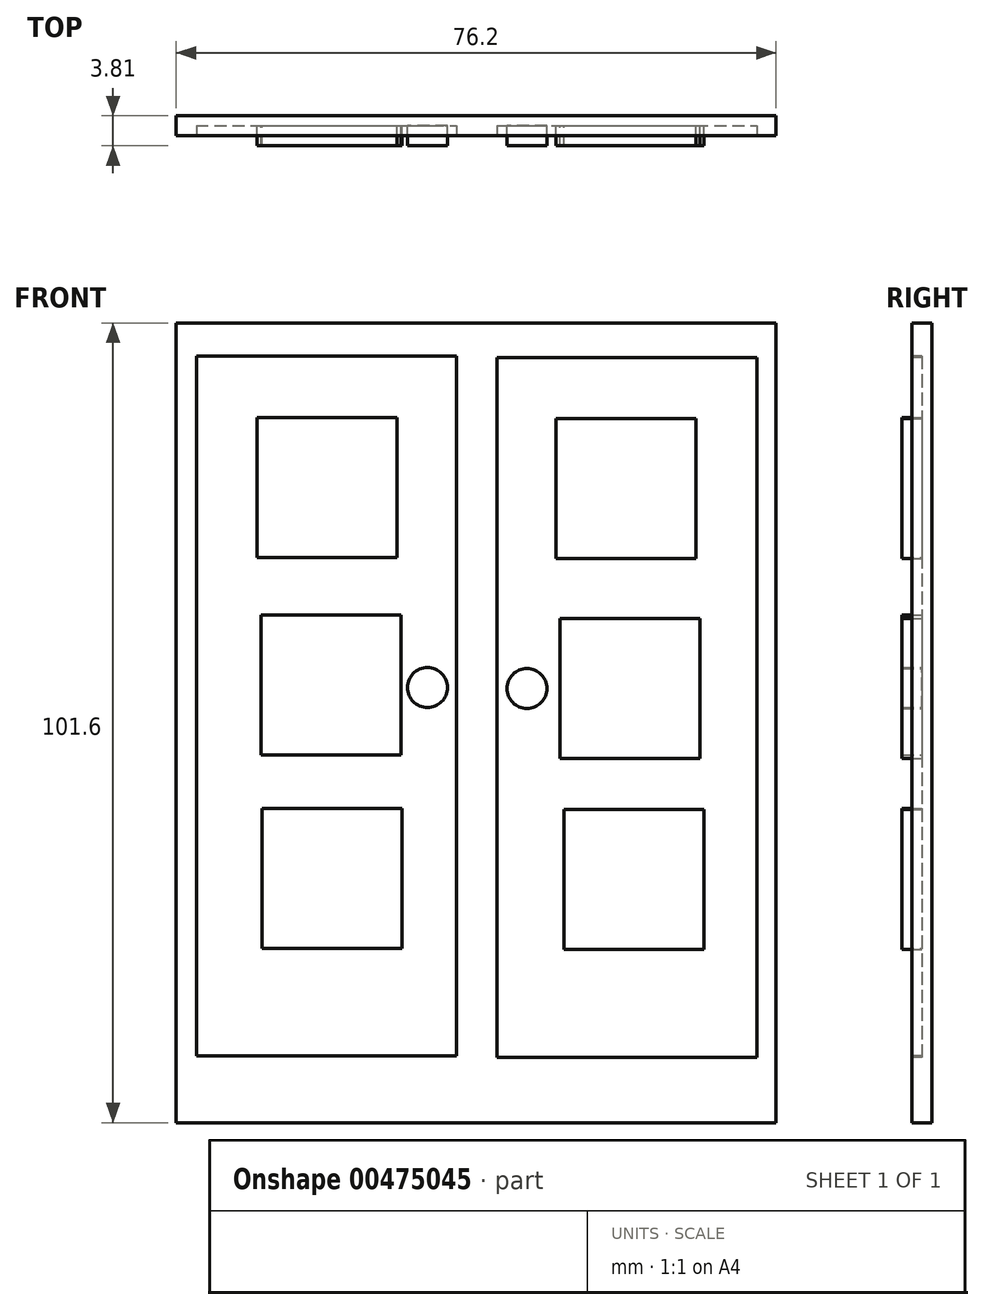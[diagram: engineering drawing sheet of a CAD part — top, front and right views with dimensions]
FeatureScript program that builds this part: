
annotation { "Feature Type Name" : "Feature", "Feature Type Description" : "" }
export const myFeature = defineFeature(function(context is Context, id is Id, definition is map)
    precondition{}
    {
        {
            var Q0;
            Q0=qCreatedBy(makeId("Front.planeOp"),FACE);
            var sketch = newSketch(context, id + "F0", { "sketchPlane" : qUnion([Q0])});
            skLineSegment(sketch, "E0.bottom", {"start": v(-36.76, -60.42) * mm, "end": v(39.44, -60.42) * mm});
            skLineSegment(sketch, "E0.top", {"start": v(-36.76, 41.18) * mm, "end": v(39.44, 41.18) * mm});
            skLineSegment(sketch, "E0.left", {"start": v(-36.76, -60.42) * mm, "end": v(-36.76, 41.18) * mm});
            skLineSegment(sketch, "E0.right", {"start": v(39.44, -60.42) * mm, "end": v(39.44, 41.18) * mm});
            skSolve(sketch);
        }
        {
            var Q0;
            Q0=qSketchRegion(id+"F0",true);
            extrude(context, id + "F1", {"entities" : qUnion([Q0]), "depth" : 2.54 * mm});
        }
        {
            var Q0;
            Q0=makeQuery(id+"F1.opExtrude","CAP_FACE",FACE,{"disambiguationData":[OSD([sQuery(id+"F0.wireOp",EDGE,"E0.bottom"),sQuery(id+"F0.wireOp",EDGE,"E0.top"),sQuery(id+"F0.wireOp",EDGE,"E0.left"),sQuery(id+"F0.wireOp",EDGE,"E0.right")])],"isStart":false});
            var sketch = newSketch(context, id + "F2", { "sketchPlane" : qUnion([Q0])});
            skLineSegment(sketch, "E1.bottom", {"start": v(-34.19, 36.95) * mm, "end": v(-1.17, 36.95) * mm});
            skLineSegment(sketch, "E1.top", {"start": v(-34.19, -51.95) * mm, "end": v(-1.17, -51.95) * mm});
            skLineSegment(sketch, "E1.left", {"start": v(-34.19, 36.95) * mm, "end": v(-34.19, -51.95) * mm});
            skLineSegment(sketch, "E1.right", {"start": v(-1.17, 36.95) * mm, "end": v(-1.17, -51.95) * mm});
            skLineSegment(sketch, "E2.bottom", {"start": v(4.02, 36.78) * mm, "end": v(37.04, 36.78) * mm});
            skLineSegment(sketch, "E2.top", {"start": v(4.02, -52.12) * mm, "end": v(37.04, -52.12) * mm});
            skLineSegment(sketch, "E2.left", {"start": v(4.02, 36.78) * mm, "end": v(4.02, -52.12) * mm});
            skLineSegment(sketch, "E2.right", {"start": v(37.04, 36.78) * mm, "end": v(37.04, -52.12) * mm});
            skSolve(sketch);
        }
        {
            var Q0;
            Q0=qSketchRegion(id+"F2",true);
            extrude(context, id + "F3", {"entities" : qUnion([Q0]), "operationType" : NewBodyOperationType.REMOVE, "oppositeDirection" : true, "depth" : 1.27 * mm});
        }
        {
            var Q0;
            Q0=makeQuery(id+"F3.boolean.opBoolean","COPY",FACE,{"derivedFrom":makeQuery(id+"F3.opExtrude","CAP_FACE",FACE,{"disambiguationData":[OSD([sQuery(id+"F2.wireOp",EDGE,"E1.bottom"),sQuery(id+"F2.wireOp",EDGE,"E1.top"),sQuery(id+"F2.wireOp",EDGE,"E1.left"),sQuery(id+"F2.wireOp",EDGE,"E1.right")])],"isStart":false})});
            var sketch = newSketch(context, id + "F4", { "sketchPlane" : qUnion([Q0])});
            skLineSegment(sketch, "E3.bottom", {"start": v(-26.51, 29.17) * mm, "end": v(-8.73, 29.17) * mm});
            skLineSegment(sketch, "E3.top", {"start": v(-26.51, 11.4) * mm, "end": v(-8.73, 11.4) * mm});
            skLineSegment(sketch, "E3.left", {"start": v(-26.51, 29.17) * mm, "end": v(-26.51, 11.4) * mm});
            skLineSegment(sketch, "E3.right", {"start": v(-8.73, 29.17) * mm, "end": v(-8.73, 11.4) * mm});
            skLineSegment(sketch, "E4.bottom", {"start": v(-25.96, 4.06) * mm, "end": v(-8.18, 4.06) * mm});
            skLineSegment(sketch, "E4.top", {"start": v(-25.96, -13.72) * mm, "end": v(-8.18, -13.72) * mm});
            skLineSegment(sketch, "E4.left", {"start": v(-25.96, 4.06) * mm, "end": v(-25.96, -13.72) * mm});
            skLineSegment(sketch, "E4.right", {"start": v(-8.18, 4.06) * mm, "end": v(-8.18, -13.72) * mm});
            skLineSegment(sketch, "E5.bottom", {"start": v(-25.85, -20.52) * mm, "end": v(-8.07, -20.52) * mm});
            skLineSegment(sketch, "E5.top", {"start": v(-25.85, -38.3) * mm, "end": v(-8.07, -38.3) * mm});
            skLineSegment(sketch, "E5.left", {"start": v(-25.85, -20.52) * mm, "end": v(-25.85, -38.3) * mm});
            skLineSegment(sketch, "E5.right", {"start": v(-8.07, -20.52) * mm, "end": v(-8.07, -38.3) * mm});
            skLineSegment(sketch, "E6.bottom", {"start": v(11.5, 29.02) * mm, "end": v(29.28, 29.02) * mm});
            skLineSegment(sketch, "E6.top", {"start": v(11.5, 11.24) * mm, "end": v(29.28, 11.24) * mm});
            skLineSegment(sketch, "E6.left", {"start": v(11.5, 29.02) * mm, "end": v(11.5, 11.24) * mm});
            skLineSegment(sketch, "E6.right", {"start": v(29.28, 29.02) * mm, "end": v(29.28, 11.24) * mm});
            skLineSegment(sketch, "E7.bottom", {"start": v(12.02, 3.63) * mm, "end": v(29.8, 3.63) * mm});
            skLineSegment(sketch, "E7.top", {"start": v(12.02, -14.15) * mm, "end": v(29.8, -14.15) * mm});
            skLineSegment(sketch, "E7.left", {"start": v(12.02, 3.63) * mm, "end": v(12.02, -14.15) * mm});
            skLineSegment(sketch, "E7.right", {"start": v(29.8, 3.63) * mm, "end": v(29.8, -14.15) * mm});
            skLineSegment(sketch, "E8.bottom", {"start": v(12.5, -20.61) * mm, "end": v(30.29, -20.61) * mm});
            skLineSegment(sketch, "E8.top", {"start": v(12.5, -38.4) * mm, "end": v(30.29, -38.4) * mm});
            skLineSegment(sketch, "E8.left", {"start": v(12.5, -20.61) * mm, "end": v(12.5, -38.4) * mm});
            skLineSegment(sketch, "E8.right", {"start": v(30.29, -20.61) * mm, "end": v(30.29, -38.4) * mm});
            skSolve(sketch);
        }
        {
            var Q0;
            Q0=qSketchRegion(id+"F4",true);
            extrude(context, id + "F5", {"entities" : qUnion([Q0]), "operationType" : NewBodyOperationType.ADD, "depth" : 2.54 * mm});
        }
        {
            var Q0;
            Q0=makeQuery(id+"F3.boolean.opBoolean","COPY",FACE,{"derivedFrom":makeQuery(id+"F3.opExtrude","CAP_FACE",FACE,{"disambiguationData":[OSD([sQuery(id+"F2.wireOp",EDGE,"E2.bottom"),sQuery(id+"F2.wireOp",EDGE,"E2.top"),sQuery(id+"F2.wireOp",EDGE,"E2.left"),sQuery(id+"F2.wireOp",EDGE,"E2.right")])],"isStart":false})});
            var sketch = newSketch(context, id + "F6", { "sketchPlane" : qUnion([Q0])});
            skCircle(sketch, "E9", {"center": v(-4.85, -5.15) * mm, "radius": 2.54 * mm});
            skCircle(sketch, "E10", {"center": v(7.8, -5.26) * mm, "radius": 2.54 * mm});
            skPoint(sketch, "E10.centerSnap0", {"position": v(12.02, -5.26) * mm});
            skSolve(sketch);
        }
        {
            var Q0;
            Q0=qSketchRegion(id+"F6",true);
            extrude(context, id + "F7", {"entities" : qUnion([Q0]), "operationType" : NewBodyOperationType.ADD, "depth" : 2.54 * mm});
        }
    });
